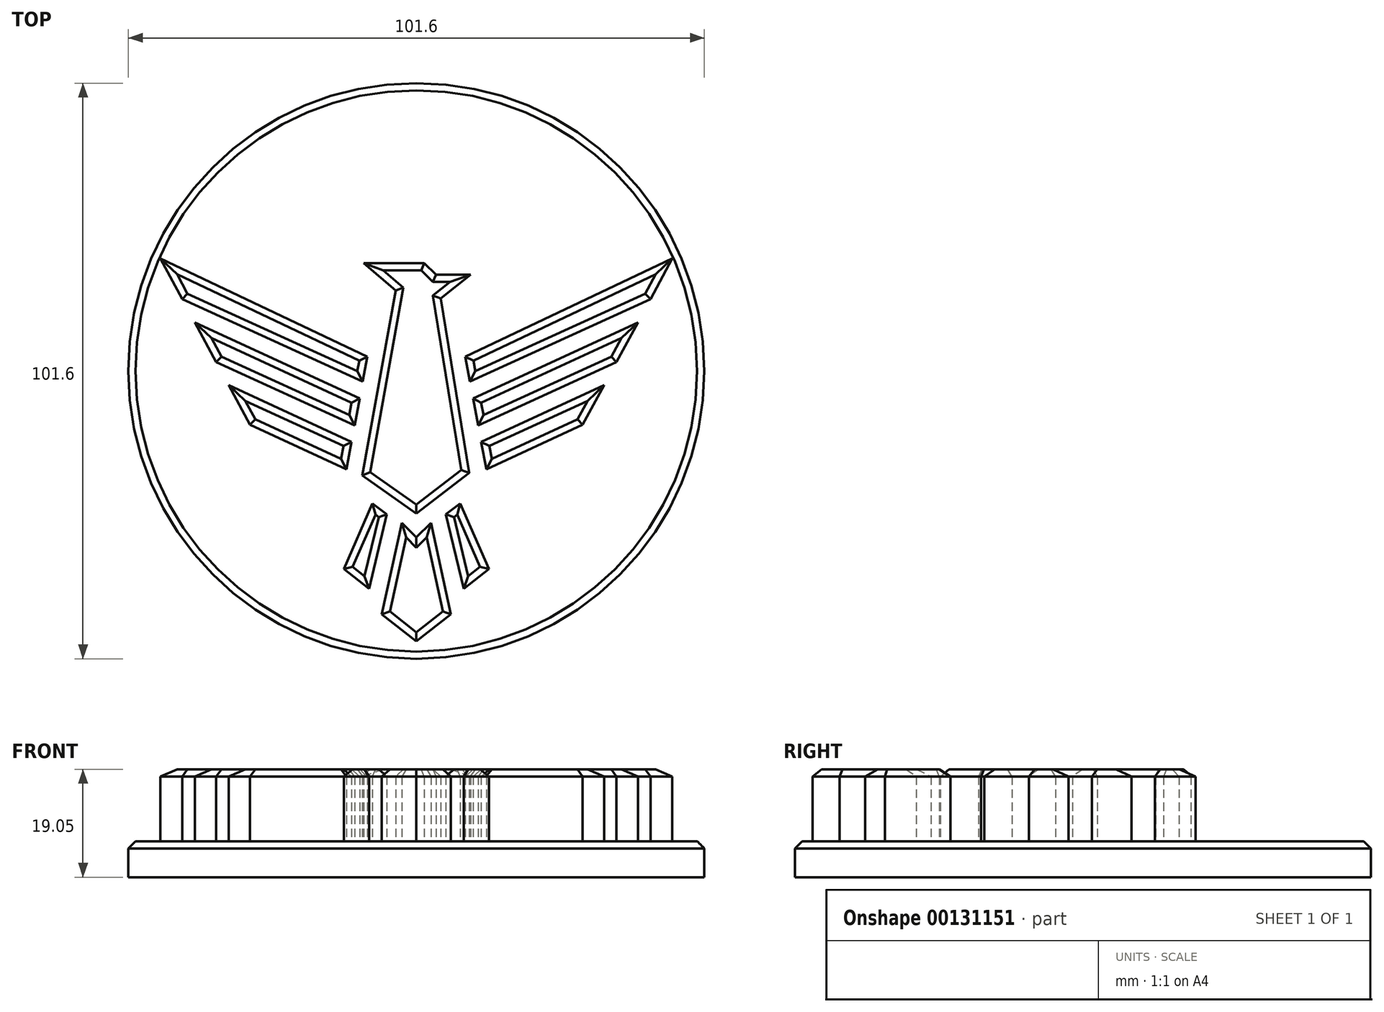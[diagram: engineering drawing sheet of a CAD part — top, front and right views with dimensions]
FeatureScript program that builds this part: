
annotation { "Feature Type Name" : "Feature", "Feature Type Description" : "" }
export const myFeature = defineFeature(function(context is Context, id is Id, definition is map)
    precondition{}
    {
        {
            var Q0;
            Q0=qCreatedBy(makeId("Top.planeOp"),FACE);
            var sketch = newSketch(context, id + "F0", { "sketchPlane" : qUnion([Q0])});
            skLineSegment(sketch, "E0", {"start": v(0, -63.96) * mm, "end": v(0, 27.01) * mm});
            skLineSegment(sketch, "E1", {"start": v(-8.64, 0) * mm, "end": v(-45.16, 17.3) * mm});
            skLineSegment(sketch, "E2", {"start": v(-45.16, 17.3) * mm, "end": v(-41.3, 10.12) * mm});
            skLineSegment(sketch, "E3", {"start": v(-29.34, -12.06) * mm, "end": v(-12.34, -19.94) * mm});
            skLineSegment(sketch, "E4", {"start": v(-12.34, -19.94) * mm, "end": v(-11.43, -15.07) * mm});
            skLineSegment(sketch, "E5", {"start": v(-9.46, -4.41) * mm, "end": v(-41.3, 10.12) * mm});
            skLineSegment(sketch, "E6", {"start": v(-10.01, -7.4) * mm, "end": v(-39.08, 6.02) * mm});
            skLineSegment(sketch, "E7", {"start": v(-10.9, -12.17) * mm, "end": v(-35.31, -0.98) * mm});
            skLineSegment(sketch, "E8", {"start": v(-11.43, -15.07) * mm, "end": v(-33.1, -5.07) * mm});
            skLineSegment(sketch, "E9.trimOffspring", {"start": v(-39.08, 6.02) * mm, "end": v(-35.31, -0.98) * mm});
            skLineSegment(sketch, "E10.trimOffspring", {"start": v(-33.1, -5.07) * mm, "end": v(-29.34, -12.06) * mm});
            skLineSegment(sketch, "E11.trimOffspring", {"start": v(-10.9, -12.17) * mm, "end": v(-10.01, -7.4) * mm});
            skLineSegment(sketch, "E12.trimOffspring", {"start": v(-9.46, -4.41) * mm, "end": v(-8.64, 0) * mm});
            skLineSegment(sketch, "E13", {"start": v(0, -31.93) * mm, "end": v(-2.56, -29.38) * mm});
            skLineSegment(sketch, "E14", {"start": v(-2.56, -29.38) * mm, "end": v(-6.09, -45.47) * mm});
            skLineSegment(sketch, "E15", {"start": v(-6.09, -45.47) * mm, "end": v(0, -50.25) * mm});
            skLineSegment(sketch, "E16", {"start": v(-7.74, -25.94) * mm, "end": v(-5.2, -27.86) * mm});
            skLineSegment(sketch, "E17", {"start": v(-5.2, -27.86) * mm, "end": v(-8.37, -41) * mm});
            skLineSegment(sketch, "E18", {"start": v(-8.37, -41) * mm, "end": v(-12.8, -37.47) * mm});
            skLineSegment(sketch, "E19", {"start": v(-12.8, -37.47) * mm, "end": v(-7.74, -25.94) * mm});
            skLineSegment(sketch, "E20.MirrorCS", {"start": v(9.46, -4.41) * mm, "end": v(8.64, 0) * mm});
            skLineSegment(sketch, "E21.MirrorCS", {"start": v(10.9, -12.17) * mm, "end": v(10.01, -7.4) * mm});
            skLineSegment(sketch, "E22.MirrorCS", {"start": v(12.8, -37.47) * mm, "end": v(7.74, -25.94) * mm});
            skLineSegment(sketch, "E23.MirrorCS", {"start": v(5.2, -27.86) * mm, "end": v(8.37, -41) * mm});
            skLineSegment(sketch, "E24.MirrorCS", {"start": v(33.1, -5.07) * mm, "end": v(29.34, -12.06) * mm});
            skLineSegment(sketch, "E25.MirrorCS", {"start": v(10.9, -12.17) * mm, "end": v(35.31, -0.98) * mm});
            skLineSegment(sketch, "E26.MirrorCS", {"start": v(7.74, -25.94) * mm, "end": v(5.2, -27.86) * mm});
            skLineSegment(sketch, "E27.MirrorCS", {"start": v(10.01, -7.4) * mm, "end": v(39.08, 6.02) * mm});
            skLineSegment(sketch, "E28.MirrorCS", {"start": v(11.43, -15.07) * mm, "end": v(33.1, -5.07) * mm});
            skLineSegment(sketch, "E29.MirrorCS", {"start": v(9.46, -4.41) * mm, "end": v(41.3, 10.12) * mm});
            skLineSegment(sketch, "E30.MirrorCS", {"start": v(0, -31.93) * mm, "end": v(2.56, -29.38) * mm});
            skLineSegment(sketch, "E31.MirrorCS", {"start": v(29.34, -12.06) * mm, "end": v(12.34, -19.94) * mm});
            skLineSegment(sketch, "E32.MirrorCS", {"start": v(45.16, 17.3) * mm, "end": v(41.3, 10.12) * mm});
            skLineSegment(sketch, "E33.MirrorCS", {"start": v(39.08, 6.02) * mm, "end": v(35.31, -0.98) * mm});
            skLineSegment(sketch, "E34.MirrorCS", {"start": v(12.34, -19.94) * mm, "end": v(11.43, -15.07) * mm});
            skLineSegment(sketch, "E35.MirrorCS", {"start": v(8.64, 0) * mm, "end": v(45.16, 17.3) * mm});
            skLineSegment(sketch, "E36.MirrorCS", {"start": v(8.37, -41) * mm, "end": v(12.8, -37.47) * mm});
            skLineSegment(sketch, "E37.MirrorCS", {"start": v(6.09, -45.47) * mm, "end": v(0, -50.25) * mm});
            skLineSegment(sketch, "E38.MirrorCS", {"start": v(2.56, -29.38) * mm, "end": v(6.09, -45.47) * mm});
            skLineSegment(sketch, "E39", {"start": v(-9.27, 16.5) * mm, "end": v(1.38, 16.5) * mm});
            skLineSegment(sketch, "E40", {"start": v(1.38, 16.5) * mm, "end": v(3.46, 14.42) * mm});
            skLineSegment(sketch, "E41", {"start": v(3.46, 14.42) * mm, "end": v(9.6, 14.42) * mm});
            skLineSegment(sketch, "E42", {"start": v(9.6, 14.42) * mm, "end": v(4.3, 10.25) * mm});
            skLineSegment(sketch, "E43", {"start": v(4.3, 10.25) * mm, "end": v(9.32, -20.56) * mm});
            skLineSegment(sketch, "E44", {"start": v(9.32, -20.56) * mm, "end": v(0, -27.73) * mm});
            skLineSegment(sketch, "E45", {"start": v(0, -27.73) * mm, "end": v(-9.56, -20.98) * mm});
            skLineSegment(sketch, "E46", {"start": v(-9.56, -20.98) * mm, "end": v(-3.65, 11.68) * mm});
            skLineSegment(sketch, "E47", {"start": v(-3.65, 11.68) * mm, "end": v(-9.27, 16.5) * mm});
            skSolve(sketch);
        }
        {
            var Q0;
            Q0=qCreatedBy(makeId("Top.planeOp"),FACE);
            var sketch = newSketch(context, id + "F1", { "sketchPlane" : qUnion([Q0])});
            skCircle(sketch, "E48", {"center": v(0, -2.54) * mm, "radius": 50.8 * mm});
            skSolve(sketch);
        }
        {
            var Q0;
            Q0 = qSketchRegion(id + "F1", true);
            extrude(context, id + "F2", {"entities" : qUnion([Q0]), "oppositeDirection" : true, "depth" : 6.35 * mm});
        }
        {
            var Q0;
            Q0 = qSketchRegion(id + "F0", true);
            extrude(context, id + "F3", {"entities" : qUnion([Q0]), "operationType" : NewBodyOperationType.ADD, "depth" : 12.7 * mm});
        }
        {
            var Q0;
            Q0=makeQuery(id+"F3.opExtrude","CAP_EDGE",EDGE,{"disambiguationData":[OSD([sQuery(id+"F0.wireOp",EDGE,"E1")])],"isStart":false});
            var Q1;
            Q1=makeQuery(id+"F3.opExtrude","CAP_EDGE",EDGE,{"disambiguationData":[OSD([sQuery(id+"F0.wireOp",EDGE,"E2")])],"isStart":false});
            var Q2;
            Q2=makeQuery(id+"F3.opExtrude","CAP_EDGE",EDGE,{"disambiguationData":[OSD([sQuery(id+"F0.wireOp",EDGE,"E12.trimOffspring")])],"isStart":false});
            var Q3;
            Q3=makeQuery(id+"F3.opExtrude","CAP_EDGE",EDGE,{"disambiguationData":[OSD([sQuery(id+"F0.wireOp",EDGE,"E5")])],"isStart":false});
            var Q4;
            Q4=makeQuery(id+"F3.opExtrude","CAP_EDGE",EDGE,{"disambiguationData":[OSD([sQuery(id+"F0.wireOp",EDGE,"E6")])],"isStart":false});
            var Q5;
            Q5=makeQuery(id+"F3.opExtrude","CAP_EDGE",EDGE,{"disambiguationData":[OSD([sQuery(id+"F0.wireOp",EDGE,"E11.trimOffspring")])],"isStart":false});
            var Q6;
            Q6=makeQuery(id+"F3.opExtrude","CAP_EDGE",EDGE,{"disambiguationData":[OSD([sQuery(id+"F0.wireOp",EDGE,"E7")])],"isStart":false});
            var Q7;
            Q7=makeQuery(id+"F3.opExtrude","CAP_EDGE",EDGE,{"disambiguationData":[OSD([sQuery(id+"F0.wireOp",EDGE,"E9.trimOffspring")])],"isStart":false});
            var Q8;
            Q8=makeQuery(id+"F3.opExtrude","CAP_EDGE",EDGE,{"disambiguationData":[OSD([sQuery(id+"F0.wireOp",EDGE,"E10.trimOffspring")])],"isStart":false});
            var Q9;
            Q9=makeQuery(id+"F3.opExtrude","CAP_EDGE",EDGE,{"disambiguationData":[OSD([sQuery(id+"F0.wireOp",EDGE,"E8")])],"isStart":false});
            var Q10;
            Q10=makeQuery(id+"F3.opExtrude","CAP_EDGE",EDGE,{"disambiguationData":[OSD([sQuery(id+"F0.wireOp",EDGE,"E3")])],"isStart":false});
            var Q11;
            Q11=makeQuery(id+"F3.opExtrude","CAP_EDGE",EDGE,{"disambiguationData":[OSD([sQuery(id+"F0.wireOp",EDGE,"E4")])],"isStart":false});
            var Q12;
            Q12=makeQuery(id+"F3.opExtrude","CAP_EDGE",EDGE,{"disambiguationData":[OSD([sQuery(id+"F0.wireOp",EDGE,"E20.MirrorCS")])],"isStart":false});
            var Q13;
            Q13=makeQuery(id+"F3.opExtrude","CAP_EDGE",EDGE,{"disambiguationData":[OSD([sQuery(id+"F0.wireOp",EDGE,"E35.MirrorCS")])],"isStart":false});
            var Q14;
            Q14=makeQuery(id+"F3.opExtrude","CAP_EDGE",EDGE,{"disambiguationData":[OSD([sQuery(id+"F0.wireOp",EDGE,"E29.MirrorCS")])],"isStart":false});
            var Q15;
            Q15=makeQuery(id+"F3.opExtrude","CAP_EDGE",EDGE,{"disambiguationData":[OSD([sQuery(id+"F0.wireOp",EDGE,"E32.MirrorCS")])],"isStart":false});
            var Q16;
            Q16=makeQuery(id+"F3.opExtrude","CAP_EDGE",EDGE,{"disambiguationData":[OSD([sQuery(id+"F0.wireOp",EDGE,"E21.MirrorCS")])],"isStart":false});
            var Q17;
            Q17=makeQuery(id+"F3.opExtrude","CAP_EDGE",EDGE,{"disambiguationData":[OSD([sQuery(id+"F0.wireOp",EDGE,"E27.MirrorCS")])],"isStart":false});
            var Q18;
            Q18=makeQuery(id+"F3.opExtrude","CAP_EDGE",EDGE,{"disambiguationData":[OSD([sQuery(id+"F0.wireOp",EDGE,"E25.MirrorCS")])],"isStart":false});
            var Q19;
            Q19=makeQuery(id+"F3.opExtrude","CAP_EDGE",EDGE,{"disambiguationData":[OSD([sQuery(id+"F0.wireOp",EDGE,"E33.MirrorCS")])],"isStart":false});
            var Q20;
            Q20=makeQuery(id+"F3.opExtrude","CAP_EDGE",EDGE,{"disambiguationData":[OSD([sQuery(id+"F0.wireOp",EDGE,"E34.MirrorCS")])],"isStart":false});
            var Q21;
            Q21=makeQuery(id+"F3.opExtrude","CAP_EDGE",EDGE,{"disambiguationData":[OSD([sQuery(id+"F0.wireOp",EDGE,"E28.MirrorCS")])],"isStart":false});
            var Q22;
            Q22=makeQuery(id+"F3.opExtrude","CAP_EDGE",EDGE,{"disambiguationData":[OSD([sQuery(id+"F0.wireOp",EDGE,"E24.MirrorCS")])],"isStart":false});
            var Q23;
            Q23=makeQuery(id+"F3.opExtrude","CAP_EDGE",EDGE,{"disambiguationData":[OSD([sQuery(id+"F0.wireOp",EDGE,"E31.MirrorCS")])],"isStart":false});
            var Q24;
            Q24=makeQuery(id+"F3.opExtrude","CAP_EDGE",EDGE,{"disambiguationData":[OSD([sQuery(id+"F0.wireOp",EDGE,"E19")])],"isStart":false});
            var Q25;
            Q25=makeQuery(id+"F3.opExtrude","CAP_EDGE",EDGE,{"disambiguationData":[OSD([sQuery(id+"F0.wireOp",EDGE,"E16")])],"isStart":false});
            var Q26;
            Q26=makeQuery(id+"F3.opExtrude","CAP_EDGE",EDGE,{"disambiguationData":[OSD([sQuery(id+"F0.wireOp",EDGE,"E17")])],"isStart":false});
            var Q27;
            Q27=makeQuery(id+"F3.opExtrude","CAP_EDGE",EDGE,{"disambiguationData":[OSD([sQuery(id+"F0.wireOp",EDGE,"E18")])],"isStart":false});
            var Q28;
            Q28=makeQuery(id+"F3.opExtrude","CAP_EDGE",EDGE,{"disambiguationData":[OSD([sQuery(id+"F0.wireOp",EDGE,"E15")])],"isStart":false});
            var Q29;
            Q29=makeQuery(id+"F3.opExtrude","CAP_EDGE",EDGE,{"disambiguationData":[OSD([sQuery(id+"F0.wireOp",EDGE,"E37.MirrorCS")])],"isStart":false});
            var Q30;
            Q30=makeQuery(id+"F3.opExtrude","CAP_EDGE",EDGE,{"disambiguationData":[OSD([sQuery(id+"F0.wireOp",EDGE,"E38.MirrorCS")])],"isStart":false});
            var Q31;
            Q31=makeQuery(id+"F3.opExtrude","CAP_EDGE",EDGE,{"disambiguationData":[OSD([sQuery(id+"F0.wireOp",EDGE,"E14")])],"isStart":false});
            var Q32;
            Q32=makeQuery(id+"F3.opExtrude","CAP_EDGE",EDGE,{"disambiguationData":[OSD([sQuery(id+"F0.wireOp",EDGE,"E13")])],"isStart":false});
            var Q33;
            Q33=makeQuery(id+"F3.opExtrude","CAP_EDGE",EDGE,{"disambiguationData":[OSD([sQuery(id+"F0.wireOp",EDGE,"E30.MirrorCS")])],"isStart":false});
            var Q34;
            Q34=makeQuery(id+"F3.opExtrude","CAP_EDGE",EDGE,{"disambiguationData":[OSD([sQuery(id+"F0.wireOp",EDGE,"E23.MirrorCS")])],"isStart":false});
            var Q35;
            Q35=makeQuery(id+"F3.opExtrude","CAP_EDGE",EDGE,{"disambiguationData":[OSD([sQuery(id+"F0.wireOp",EDGE,"E26.MirrorCS")])],"isStart":false});
            var Q36;
            Q36=makeQuery(id+"F3.opExtrude","CAP_EDGE",EDGE,{"disambiguationData":[OSD([sQuery(id+"F0.wireOp",EDGE,"E22.MirrorCS")])],"isStart":false});
            var Q37;
            Q37=makeQuery(id+"F3.opExtrude","CAP_EDGE",EDGE,{"disambiguationData":[OSD([sQuery(id+"F0.wireOp",EDGE,"E36.MirrorCS")])],"isStart":false});
            var Q38;
            Q38=makeQuery(id+"F3.opExtrude","CAP_EDGE",EDGE,{"disambiguationData":[OSD([sQuery(id+"F0.wireOp",EDGE,"E45")])],"isStart":false});
            var Q39;
            Q39=makeQuery(id+"F3.opExtrude","CAP_EDGE",EDGE,{"disambiguationData":[OSD([sQuery(id+"F0.wireOp",EDGE,"E44")])],"isStart":false});
            var Q40;
            Q40=makeQuery(id+"F3.opExtrude","CAP_EDGE",EDGE,{"disambiguationData":[OSD([sQuery(id+"F0.wireOp",EDGE,"E46")])],"isStart":false});
            var Q41;
            Q41=makeQuery(id+"F3.opExtrude","CAP_EDGE",EDGE,{"disambiguationData":[OSD([sQuery(id+"F0.wireOp",EDGE,"E43")])],"isStart":false});
            var Q42;
            Q42=makeQuery(id+"F3.opExtrude","CAP_EDGE",EDGE,{"disambiguationData":[OSD([sQuery(id+"F0.wireOp",EDGE,"E47")])],"isStart":false});
            var Q43;
            Q43=makeQuery(id+"F3.opExtrude","CAP_EDGE",EDGE,{"disambiguationData":[OSD([sQuery(id+"F0.wireOp",EDGE,"E39")])],"isStart":false});
            var Q44;
            Q44=makeQuery(id+"F3.opExtrude","CAP_EDGE",EDGE,{"disambiguationData":[OSD([sQuery(id+"F0.wireOp",EDGE,"E40")])],"isStart":false});
            var Q45;
            Q45=makeQuery(id+"F3.opExtrude","CAP_EDGE",EDGE,{"disambiguationData":[OSD([sQuery(id+"F0.wireOp",EDGE,"E41")])],"isStart":false});
            var Q46;
            Q46=makeQuery(id+"F3.opExtrude","CAP_EDGE",EDGE,{"disambiguationData":[OSD([sQuery(id+"F0.wireOp",EDGE,"E42")])],"isStart":false});
            var Q47;
            Q47=makeQuery(id+"F2.opExtrude","CAP_EDGE",EDGE,{"disambiguationData":[OSD([sQuery(id+"F1.wireOp",EDGE,"E48")])],"isStart":true});
            chamfer(context, id + "F4", {"entities" : qUnion([Q0, Q1, Q2, Q3, Q4, Q5, Q6, Q7, Q8, Q9, Q10, Q11, Q12, Q13, Q14, Q15, Q16, Q17, Q18, Q19, Q20, Q21, Q22, Q23, Q24, Q25, Q26, Q27, Q28, Q29, Q30, Q31, Q32, Q33, Q34, Q35, Q36, Q37, Q38, Q39, Q40, Q41, Q42, Q43, Q44, Q45, Q46, Q47]), "width" : 1.27 * mm, "tangentPropagation" : true});
        }
    });
